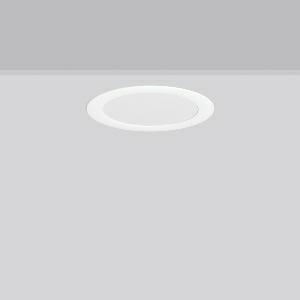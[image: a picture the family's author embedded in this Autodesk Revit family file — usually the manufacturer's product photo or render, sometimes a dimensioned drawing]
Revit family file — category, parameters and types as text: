
# Revit family: toledo_flat_round_e_672230_002_3806
name_source: partatom
category: Lighting Fixtures
units: mm (PartAtom-declared; Revit-internal decimal feet)

## family parameters
Cut with Voids When Loaded = No
Host = Face
Light Source = No
Part Type = Normal
Room Calculation Point = No
Round Connector Dimension = Use Diameter
Shared = No

## types (1)
- TOLEDO FLAT round E (1 x LED Modul 830, 1650 lm, 3000)
    Apparent Load = 17 VA
    CIE Flux Codes = 48 79 96 100 100
    Color Rendering = 80
    Color Temperature = 3000
    Default Elevation = 1800 mm
    Description = Series: TOLEDO FLAT round
Ultra thin recessed downlight. For escape route illumination. Housing: die-cast aluminium, powder-coated. Lightguide and diffuser made of non-yellowing plastic (PMMA). Diffuser opal matt plastic. Ceiling installation with spring system. Including separate LED converter with connecting cable 250 mm. Suitable for connection to central battery systems. External driver with simple plug-in locking system. 
Colour: white
Diameter: 255 mm
Height: 3 mm
Cut-out diameter: 234 mm
Recess height: 35 mm
Luminaire: recess height: 31-51 mm
Weight: 0.81 kg
Operating mode: maintained power mode
Lamp: LED
Socket: without socket
Colour temperature: 3000K
Colour rendering index (CRI): 80
System power: 17 W
Rated luminous flux: 1650 lm
Luminous flux, emergency: 1650 lm
System power, emergency: 17 W
Control gear: Regulated power supply
Protection class: II
Type of protection: IP 54
    Height = 0 mm  [stored 0 ft]
    Lamp = 1 x LED Modul 830
    Lamp Light Flux = 1650 lm
    Lamp count = 1
    Length = 255 mm
    Lifetime = 50000 h
    Luminous efficacy = 97 lm/W
    Manufacturer = RZB
    ModVariant = No
    Model = 672230.002
    Mounting Place = Ceiling
    Mounting Type = Recessed
    Number of Poles = 1
    OnlyDefault = Yes
    Power Factor = 1
    Product Name = TOLEDO FLAT round E
    Product group = Recessed downlights
    ProductGroupID = 402
    Protection Class = Protection class II
    Protection Degree = IP 40
    RLX_Detail_Level = 1
    RLX_Emergency_Light_Flux = 1650 lm
    RLX_Emergency_Type = 3
    RLX_Emergency_Type_DB = Yes
    RlxData = <blob elided: 29845 chars, md5=0532048c>
    Socket = socket
    Standby Power = 0 W
    System Light Flux = 1650 lm
    System Power = 17 W
    Type Comments = Product without accessories
    Type Image = 901453.002.jpg
    URL = http://relux.com
    VarID = ---
    Voltage = 230 V
    Voltage Range = 220-240 V
    Weight = 0.00 kg
    Width = 0 mm  [stored 0 ft]

note: [stored X ft] marks values corroborated as IEEE doubles in the binary element streams (Revit-internal decimal feet)

## geometry (parser evidence)
native form markers: Blend x4, Sweep x9
no freeform markers — native parametric forms only
